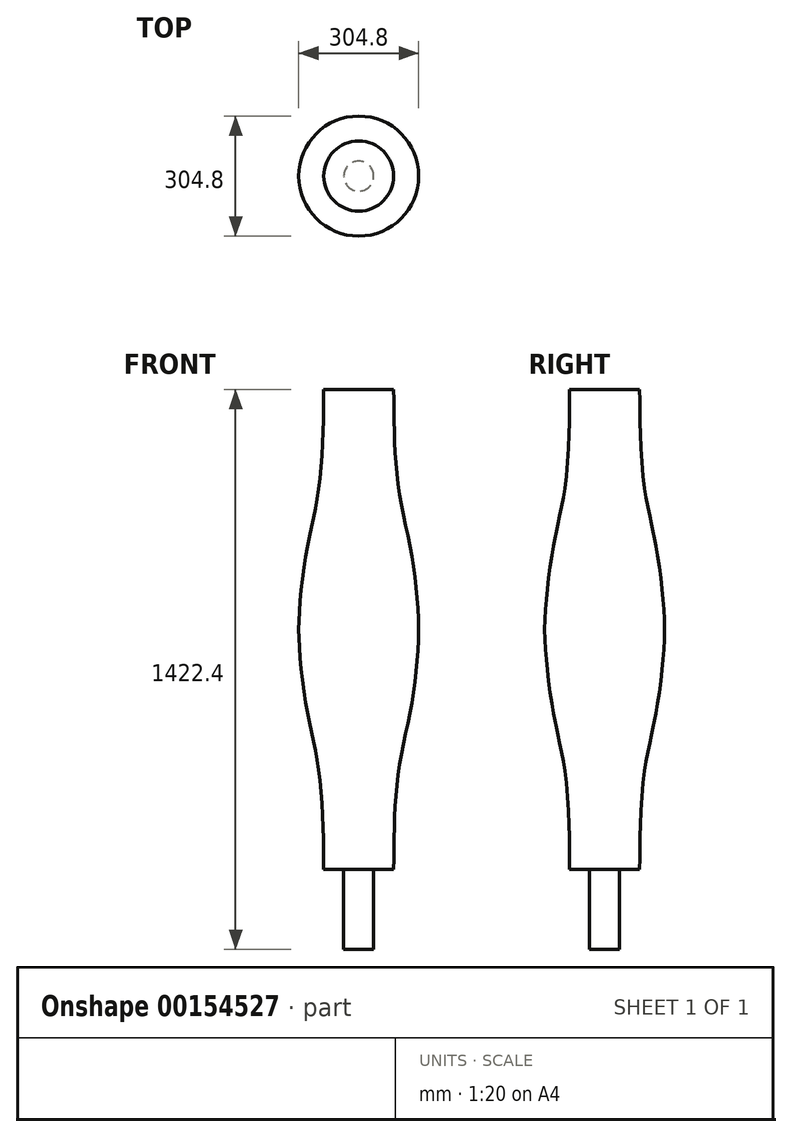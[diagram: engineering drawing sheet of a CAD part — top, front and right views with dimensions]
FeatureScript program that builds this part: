
annotation { "Feature Type Name" : "Feature", "Feature Type Description" : "" }
export const myFeature = defineFeature(function(context is Context, id is Id, definition is map)
    precondition{}
    {
        {
            var Q0;
            Q0=qCreatedBy(makeId("Front.planeOp"),FACE);
            var sketch = newSketch(context, id + "F0", { "sketchPlane" : qUnion([Q0])});
            skLineSegment(sketch, "E0", {"start": v(0, 0) * mm, "end": v(0, 1422.4) * mm});
            skLineSegment(sketch, "E1", {"start": v(-107.95, 0) * mm, "end": v(0, 0) * mm});
            skLineSegment(sketch, "E2", {"start": v(-38.1, 0) * mm, "end": v(-38.1, 203.2) * mm});
            skArc(sketch, "E3", {"start": v(-107.95, 0) * mm, "mid": v(-77.32, 31.3) * mm, "end": v(-38.1, 50.8) * mm});
            skLineSegment(sketch, "E4", {"start": v(-38.1, 203.2) * mm, "end": v(-88.9, 203.2) * mm});
            skFitSpline(sketch, "E5", {"points": [v(-88.9, 203.2) * mm, v(-98.61, 433.05) * mm, v(-131.99, 610.82) * mm, v(-152.4, 812.8) * mm], "startDerivative": vector(0, 490.93) * mm, "endDerivative": vector(0, 466.15) * mm});
            skLineSegment(sketch, "E6", {"start": v(-152.4, 812.8) * mm, "end": v(0, 812.8) * mm});
            skLineSegment(sketch, "E7", {"start": v(-88.9, 203.2) * mm, "end": v(-88.9, 137.76) * mm, "construction": true});
            skLineSegment(sketch, "E8", {"start": v(-152.4, 812.8) * mm, "end": v(-152.4, 896) * mm, "construction": true});
            skFitSpline(sketch, "E9.MirrorCS", {"points": [v(-88.9, 1422.4) * mm, v(-98.61, 1192.55) * mm, v(-131.99, 1014.78) * mm, v(-152.4, 812.8) * mm], "startDerivative": vector(0, -490.93) * mm, "endDerivative": vector(0, -466.15) * mm});
            skLineSegment(sketch, "E10", {"start": v(0, 1422.4) * mm, "end": v(-88.9, 1422.4) * mm});
            skSolve(sketch);
        }
        {
            var Q0;
            {var subQ2=sQuery(id+"F0.wireOp",EDGE,"E6");Q0=makeQuery(id+"F0.imprint","IMPRINT",FACE,{"disambiguationData":[TD([[makeQuery(id+"F0.imprint","IMPRINT",EDGE,{"derivedFrom":subQ2}),1.0]])]});}
            var Q1;
            {var subQ0=sQuery(id+"F0.wireOp",EDGE,"E4");Q1=makeQuery(id+"F0.imprint","IMPRINT",FACE,{"disambiguationData":[TD([[makeQuery(id+"F0.imprint","IMPRINT",EDGE,{"derivedFrom":subQ0}),-1.0]])]});}
            var Q2;
            {var subQ0=sQuery(id+"F0.wireOp",EDGE,"E3");Q2=makeQuery(id+"F0.imprint","IMPRINT",FACE,{"disambiguationData":[TD([[makeQuery(id+"F0.imprint","IMPRINT",EDGE,{"derivedFrom":subQ0}),-1.0]])]});}
            var Q3;
            Q3=sQuery(id+"F0.wireOp",EDGE,"E0");
            revolve(context, id + "F1", {"entities" : qUnion([Q0, Q1, Q2]), "axis" : qUnion([Q3]), "revolveType" : RevolveType.FULL});
        }
    });
